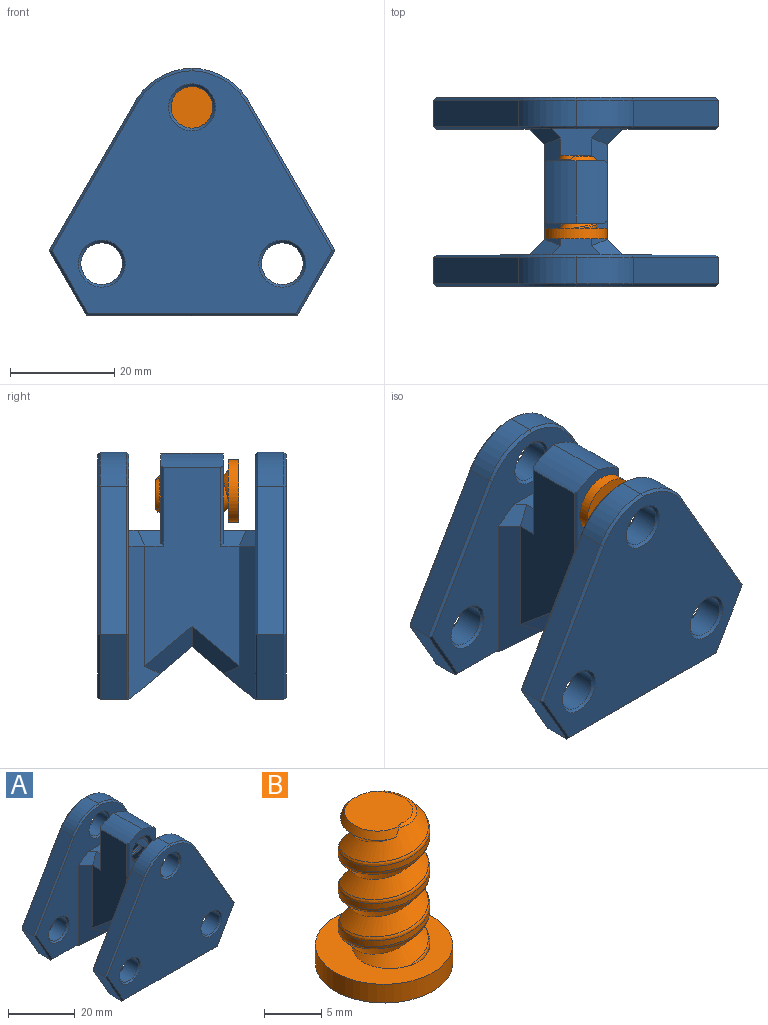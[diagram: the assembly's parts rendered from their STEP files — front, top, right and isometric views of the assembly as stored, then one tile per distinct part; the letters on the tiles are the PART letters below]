
ASSEMBLY  parts=2 mates=1
PART A: 103 faces, bbox 54.9x36.2x47.5 mm
  f0: cone r=4.5mm half-angle=45deg, axis (0,-1,0), area 27.1mm2, adj f1,f27,f100,f101,f102
  f1: plane 5.01x4.98mm, normal (0,-1,0), area 2.8mm2, adj f0
  f2: cone r=4.5mm half-angle=45deg, axis (0,1,0), area 27mm2, adj f3,f29,f100,f101,f102
  f3: plane 5.01x4.98mm, normal (0,1,0), area 2.8mm2, adj f2
  f4: plane 40.41x5.5mm, normal (0,0,-1), area 211.3mm2, adj f11,f14,f31,f34,f35,f54,f56,f92
  f5: plane 38.07x18.2mm, normal (1,0,0), area 515.3mm2, adj f32,f34,f38,f42,f44,f45,f49,f70
  f6: plane 38.07x18.2mm, normal (-1,0,0), area 515.3mm2, adj f33,f35,f36,f40,f46,f47,f48,f71
  f7: cylinder r=4mm len=8mm, axis (0,1,0), area 125.7mm2, adj f75,f99
  f8: cylinder r=4mm len=8mm, axis (0,1,0), area 125.7mm2, adj f79,f89
  f9: plane 28.5x16.45mm, normal (0.87,0,0.5), area 164.5mm2, adj f14,f51,f57,f91
  f10: plane 28.5x16.45mm, normal (-0.87,0,0.5), area 164.5mm2, adj f11,f50,f60,f96
  f11: plane 12.5x7.22mm, normal (-0.87,0,-0.5), area 72.2mm2, adj f4,f10,f58,f94
  f12: plane 40.41x5.5mm, normal (0,0,-1), area 211.3mm2, adj f18,f20,f30,f32,f33,f62,f63,f82
  f13: cylinder r=4mm len=8mm, axis (0,1,0), area 125.7mm2, adj f74,f98
  f14: plane 12.5x7.22mm, normal (0.87,0,-0.5), area 72.2mm2, adj f4,f9,f55,f90
  f15: cylinder r=4mm len=8mm, axis (0,1,0), area 125.7mm2, adj f76,f97
  f16: plane 28.5x16.45mm, normal (0.87,0,0.5), area 164.5mm2, adj f20,f53,f66,f81
  f17: plane 28.5x16.45mm, normal (-0.87,0,0.5), area 164.5mm2, adj f18,f52,f67,f86
  f18: plane 12.5x7.22mm, normal (-0.87,0,-0.5), area 72.2mm2, adj f12,f17,f65,f84
  f19: cylinder r=4mm len=8mm, axis (0,1,0), area 125.7mm2, adj f78,f88
  f20: plane 12.5x7.22mm, normal (0.87,0,-0.5), area 72.2mm2, adj f12,f16,f64,f80
  f21: cylinder r=4mm len=8mm, axis (0,1,0), area 125.7mm2, adj f77,f87
  f22: plane 53.69x46.5mm, normal (0,-1,0), area 1518.8mm2, adj f80,f81,f82,f83,f84,f85,f86,f87
  f23: plane 53.69x46.5mm, normal (0,1,0), area 1518.8mm2, adj f90,f91,f92,f93,f94,f95,f96,f97
  f24: plane 53.69x46.5mm, normal (0,-1,0), area 955.5mm2, adj f28,f34,f35,f37,f39,f54,f55,f56
  f25: plane 53.69x46.5mm, normal (0,1,0), area 955.5mm2, adj f26,f32,f33,f41,f43,f62,f63,f64
  f26: plane 9.51x6.1mm, normal (0,0,1), area 39.7mm2, adj f25,f27,f40,f41,f42,f43
  f27: plane 17.29x11mm, normal (0,-1,0), area 95mm2, adj f0,f26,f40,f42,f48,f49,f72,f73
  f28: plane 9.51x6.1mm, normal (0,0,1), area 39.7mm2, adj f24,f29,f36,f37,f38,f39
  f29: plane 17.29x11mm, normal (0,1,0), area 95mm2, adj f2,f28,f36,f38,f48,f49,f70,f71
  f30: plane 18x12.1mm, normal (0,0.64,-0.77), area 141.8mm2, adj f12,f31,f32,f33,f45,f47
  f31: plane 18x12.1mm, normal (0,-0.64,-0.77), area 141.8mm2, adj f4,f30,f34,f35,f44,f46
  f32: plane 29.5x6.5mm, normal (0.71,0.71,0), area 128.3mm2, adj f5,f12,f25,f30,f43,f45,f62
  f33: plane 29.5x6.5mm, normal (-0.71,0.71,0), area 128.3mm2, adj f6,f12,f25,f30,f41,f47,f63
  f34: plane 29.5x6.5mm, normal (0.71,-0.71,0), area 128.3mm2, adj f4,f5,f24,f31,f39,f44,f54
  f35: plane 29.5x6.5mm, normal (-0.71,-0.71,0), area 128.3mm2, adj f4,f6,f24,f31,f37,f46,f56
  f36: plane 4.84x3mm, normal (-0.71,0,0.71), area 16mm2, adj f6,f28,f29,f37,f71
  f37: plane 6x3mm, normal (-0.5,-0.5,0.71), area 14.3mm2, adj f24,f28,f35,f36
  f38: plane 4.84x3mm, normal (0.71,0,0.71), area 16mm2, adj f5,f28,f29,f39,f70
  f39: plane 6x3mm, normal (0.5,-0.5,0.71), area 14.3mm2, adj f24,f28,f34,f38
  f40: plane 4.84x3mm, normal (-0.71,0,0.71), area 16mm2, adj f6,f26,f27,f41,f73
  f41: plane 6x3mm, normal (-0.5,0.5,0.71), area 14.3mm2, adj f25,f26,f33,f40
  f42: plane 4.84x3mm, normal (0.71,0,0.71), area 16mm2, adj f5,f26,f27,f43,f72
  f43: plane 6x3mm, normal (0.5,0.5,0.71), area 14.3mm2, adj f25,f26,f32,f42
  f44: plane 9.1x9.03mm, normal (0.71,-0.45,-0.54), area 42.1mm2, adj f5,f31,f34,f45
  f45: plane 9.1x9.03mm, normal (0.71,0.45,-0.54), area 42.1mm2, adj f5,f30,f32,f44
  f46: plane 9.1x9.03mm, normal (-0.71,-0.45,-0.54), area 42.1mm2, adj f6,f31,f35,f47
  f47: plane 9.1x9.03mm, normal (-0.71,0.45,-0.54), area 42.1mm2, adj f6,f30,f33,f46
  f48: cylinder r=13mm len=12mm, axis (0,1,0), area 80mm2, adj f6,f27,f29,f49,f71,f73
  f49: cylinder r=13mm len=12mm, axis (0,-1,0), area 80mm2, adj f5,f27,f29,f48,f70,f72
  f50: cylinder r=13mm len=10.97mm, axis (0,1,0), area 66.6mm2, adj f10,f51,f61,f95
  f51: cylinder r=13mm len=10.97mm, axis (0,1,0), area 66.6mm2, adj f9,f50,f59,f93
  f52: cylinder r=13mm len=10.97mm, axis (0,1,0), area 66.6mm2, adj f17,f53,f69,f85
  f53: cylinder r=13mm len=10.97mm, axis (0,1,0), area 66.6mm2, adj f16,f52,f68,f83
  f54: plane 11.21x0.5mm, normal (0,-0.71,-0.71), area 7.6mm2, adj f4,f24,f34,f55
  f55: plane 12.5x7.51mm, normal (0.61,-0.71,-0.35), area 10mm2, adj f14,f24,f54,f57
  f56: plane 11.21x0.5mm, normal (0,-0.71,-0.71), area 7.6mm2, adj f4,f24,f35,f58
  f57: plane 28.5x16.89mm, normal (0.61,-0.71,0.35), area 23.2mm2, adj f9,f24,f55,f59
  f58: plane 12.5x7.51mm, normal (-0.61,-0.71,-0.35), area 10mm2, adj f11,f24,f56,f60
  f59: cone r=12.5mm half-angle=45deg, axis (0,1,0), area 9.2mm2, adj f24,f51,f57,f61
  f60: plane 28.5x16.89mm, normal (-0.61,-0.71,0.35), area 23.2mm2, adj f10,f24,f58,f61
  f61: cone r=12.5mm half-angle=45deg, axis (0,1,0), area 9.2mm2, adj f24,f50,f59,f60
  f62: plane 11.21x0.5mm, normal (0,0.71,-0.71), area 7.6mm2, adj f12,f25,f32,f64
  f63: plane 11.21x0.5mm, normal (0,0.71,-0.71), area 7.6mm2, adj f12,f25,f33,f65
  f64: plane 12.5x7.51mm, normal (0.61,0.71,-0.35), area 10mm2, adj f20,f25,f62,f66
  f65: plane 12.5x7.51mm, normal (-0.61,0.71,-0.35), area 10mm2, adj f18,f25,f63,f67
  f66: plane 28.5x16.89mm, normal (0.61,0.71,0.35), area 23.2mm2, adj f16,f25,f64,f68
  f67: plane 28.5x16.89mm, normal (-0.61,0.71,0.35), area 23.2mm2, adj f17,f25,f65,f69
  f68: cone r=12.5mm half-angle=45deg, axis (0,-1,0), area 9.2mm2, adj f25,f53,f66,f69
  f69: cone r=12.5mm half-angle=45deg, axis (0,-1,0), area 9.2mm2, adj f25,f52,f67,f68
  f70: plane 15.4x0.5mm, normal (0.71,0.71,0), area 10.6mm2, adj f5,f29,f38,f49
  f71: plane 15.4x0.5mm, normal (-0.71,0.71,0), area 10.6mm2, adj f6,f29,f36,f48
  f72: plane 15.4x0.5mm, normal (0.71,-0.71,0), area 10.6mm2, adj f5,f27,f42,f49
  f73: plane 15.4x0.5mm, normal (-0.71,-0.71,0), area 10.6mm2, adj f6,f27,f40,f48
  f74: cone r=4mm half-angle=45deg, axis (0,-1,0), area 18.9mm2, adj f13,f24
  f75: cone r=4.5mm half-angle=45deg, axis (0,-1,0), area 18.9mm2, adj f7,f24
  f76: cone r=4mm half-angle=45deg, axis (0,-1,0), area 18.9mm2, adj f15,f24
  f77: cone r=4.5mm half-angle=45deg, axis (0,1,0), area 18.9mm2, adj f21,f25
  f78: cone r=4.5mm half-angle=45deg, axis (0,1,0), area 18.9mm2, adj f19,f25
  f79: cone r=4mm half-angle=45deg, axis (0,1,0), area 18.9mm2, adj f8,f25
  f80: plane 12.5x7.51mm, normal (0.61,-0.71,-0.35), area 10mm2, adj f20,f22,f81,f82
  f81: plane 28.5x16.89mm, normal (0.61,-0.71,0.35), area 23.2mm2, adj f16,f22,f80,f83
  f82: plane 40.41x0.5mm, normal (0,-0.71,-0.71), area 28.4mm2, adj f12,f22,f80,f84
  f83: cone r=12.5mm half-angle=45deg, axis (0,1,0), area 9.2mm2, adj f22,f53,f81,f85
  f84: plane 12.5x7.51mm, normal (-0.61,-0.71,-0.35), area 10mm2, adj f18,f22,f82,f86
  f85: cone r=12.5mm half-angle=45deg, axis (0,1,0), area 9.2mm2, adj f22,f52,f83,f86
  f86: plane 28.5x16.89mm, normal (-0.61,-0.71,0.35), area 23.2mm2, adj f17,f22,f84,f85
  f87: cone r=4mm half-angle=45deg, axis (0,-1,0), area 18.9mm2, adj f21,f22
  f88: cone r=4mm half-angle=45deg, axis (0,-1,0), area 18.9mm2, adj f19,f22
  f89: cone r=4mm half-angle=45deg, axis (0,-1,0), area 18.9mm2, adj f8,f22
  f90: plane 12.5x7.51mm, normal (0.61,0.71,-0.35), area 10mm2, adj f14,f23,f91,f92
  f91: plane 28.5x16.89mm, normal (0.61,0.71,0.35), area 23.2mm2, adj f9,f23,f90,f93
  f92: plane 40.41x0.5mm, normal (0,0.71,-0.71), area 28.4mm2, adj f4,f23,f90,f94
  f93: cone r=12.5mm half-angle=45deg, axis (0,-1,0), area 9.2mm2, adj f23,f51,f91,f95
  f94: plane 12.5x7.51mm, normal (-0.61,0.71,-0.35), area 10mm2, adj f11,f23,f92,f96
  f95: cone r=12.5mm half-angle=45deg, axis (0,-1,0), area 9.2mm2, adj f23,f50,f93,f96
  f96: plane 28.5x16.89mm, normal (-0.61,0.71,0.35), area 23.2mm2, adj f10,f23,f94,f95
  f97: cone r=4.5mm half-angle=45deg, axis (0,1,0), area 18.9mm2, adj f15,f23
  f98: cone r=4.5mm half-angle=45deg, axis (0,1,0), area 18.9mm2, adj f13,f23
  f99: cone r=4.5mm half-angle=45deg, axis (0,1,0), area 18.9mm2, adj f7,f23
  f100: cylinder r=4.1mm len=11.2mm, axis (0,-1,0), area 44mm2, adj f0,f2,f101,f102
  f101: bspline ~11.92x8.21mm, area 31.2mm2, adj f0,f2,f100
  f102: bspline ~12.1x8.21mm, area 31.2mm2, adj f0,f2,f100
PART B: 12 faces, bbox 12.6x12.6x18.3 mm
  f0: cylinder r=6mm len=12mm, axis (0,0,-1), area 75.4mm2, adj f1,f2
  f1: plane 12.64x12.64mm, normal (0,0,1), area 74mm2, adj f0,f3,f5,f6,f10,f11
  f2: plane 12x12mm, normal (0,0,-1), area 113.1mm2, adj f0
  f3: cylinder r=4mm len=13.54mm, axis (0,0,-1), area 51.5mm2, adj f1,f8,f9,f10,f11
  f4: plane 6.05x5.79mm, normal (0,0,1), area 27.5mm2, adj f7,f8,f9
  f5: bspline ~16.83x9.24mm, area 124.2mm2, adj f1,f6,f8,f10
  f6: bspline ~17.29x9.24mm, area 130.3mm2, adj f1,f5,f7,f8,f9,f11
  f7: bspline ~6.68x3.81mm, area 2.9mm2, adj f4,f6,f8,f9
  f8: bspline ~6.6x3.62mm, area 6.8mm2, adj f3,f4,f5,f6,f7,f9,f10
  f9: cone r=3.54mm half-angle=45deg, axis (0,0,-1), area 2.5mm2, adj f3,f4,f6,f7,f8,f11
  f10: bspline ~14.01x8.01mm, area 30.5mm2, adj f1,f3,f5,f8
  f11: bspline ~14.35x8.01mm, area 31.3mm2, adj f1,f3,f6,f9
PLACE A t=(-13.75,-2.24,16.71)mm
PLACE B rot(axis=(-1,0,0),90deg) t=(-13.75,-11.24,36.71)mm
MATE fastened B.f0 <-> A.f0  axis (0,1,0) through (-13.75,-9.24,36.71)mm
